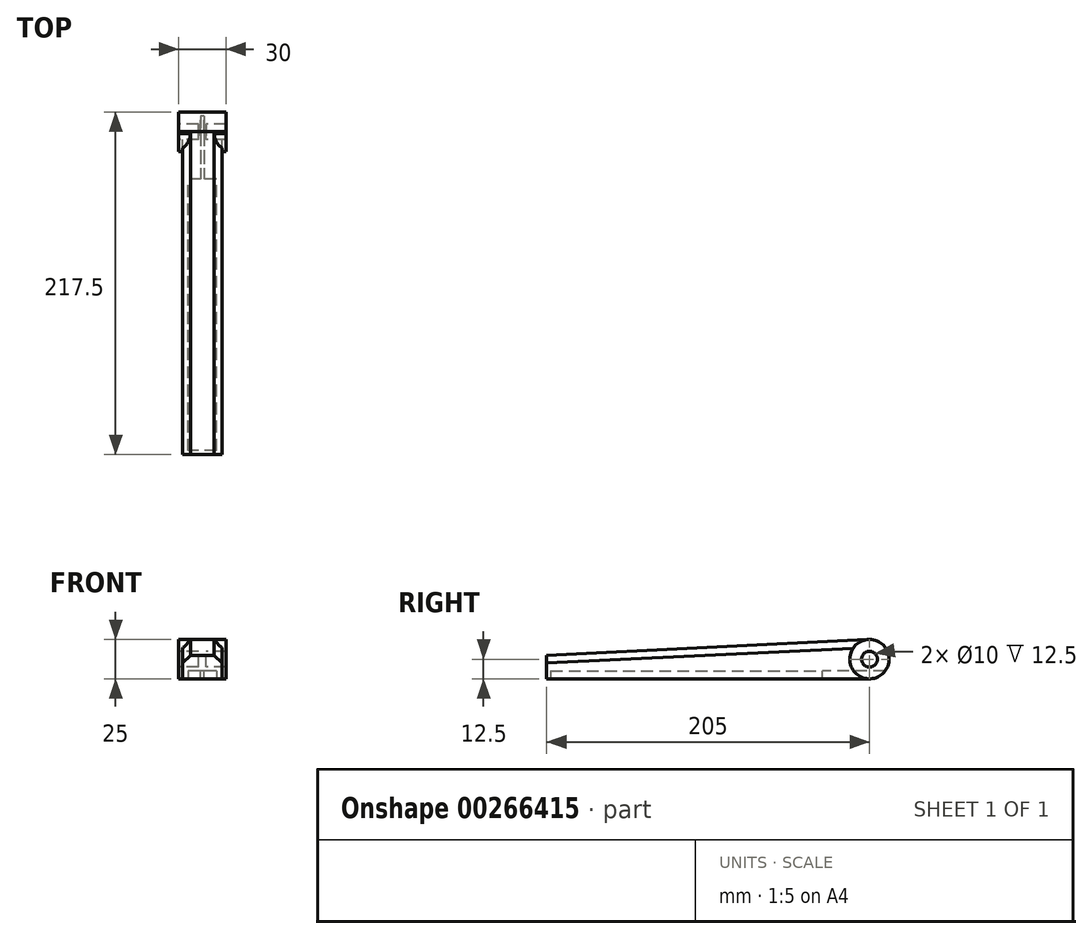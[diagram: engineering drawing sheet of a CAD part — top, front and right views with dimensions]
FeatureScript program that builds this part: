
annotation { "Feature Type Name" : "Feature", "Feature Type Description" : "" }
export const myFeature = defineFeature(function(context is Context, id is Id, definition is map)
    precondition{}
    {
        {
            var Q0;
            Q0=qCreatedBy(makeId("Right.planeOp"),FACE);
            var sketch = newSketch(context, id + "F0", { "sketchPlane" : qUnion([Q0])});
            skCircle(sketch, "E0", {"center": v(97.5, -2.5) * mm, "radius": 12.5 * mm});
            skLineSegment(sketch, "E1", {"start": v(97.5, 10) * mm, "end": v(-107.5, 0) * mm});
            skCircle(sketch, "E2", {"center": v(97.5, -2.5) * mm, "radius": 5 * mm});
            skLineSegment(sketch, "E3", {"start": v(97.5, -15) * mm, "end": v(-107.5, -15) * mm});
            skLineSegment(sketch, "E4", {"start": v(-107.5, 0) * mm, "end": v(-107.5, -15) * mm});
            skSolve(sketch);
        }
        {
            var Q0;
            Q0=makeQuery(id+"F0.imprint","IMPRINT",FACE,{"disambiguationData":[TD([[makeQuery(id+"F0.imprint","IMPRINT",EDGE,{"derivedFrom":sQuery(id+"F0.wireOp",EDGE,"E2")}),-1.0]])]});
            extrude(context, id + "F1", {"entities" : qUnion([Q0]), "depth" : 15 * mm, "hasSecondDirection" : true, "secondDirectionOppositeDirection" : true, "secondDirectionDepth" : 15 * mm, "offsetDistance" : 25 * mm});
        }
        {
            var Q0;
            {var subQ0=sQuery(id+"F0.wireOp",EDGE,"E3");Q0=makeQuery(id+"F0.imprint","IMPRINT",FACE,{"disambiguationData":[TD([[makeQuery(id+"F0.imprint","IMPRINT",EDGE,{"derivedFrom":subQ0}),-1.0]])]});}
            extrude(context, id + "F2", {"entities" : qUnion([Q0]), "operationType" : NewBodyOperationType.ADD, "depth" : 12.5 * mm, "hasSecondDirection" : true, "secondDirectionOppositeDirection" : true, "secondDirectionDepth" : 12.5 * mm, "offsetDistance" : 25 * mm});
        }
        {
            var Q0;
            Q0=makeQuery(id+"F2.opExtrude","SWEPT_FACE",FACE,{"disambiguationData":[OSD([sQuery(id+"F0.wireOp",EDGE,"E3")])]});
            var sketch = newSketch(context, id + "F3", { "sketchPlane" : qUnion([Q0])});
            skLineSegment(sketch, "E5", {"start": v(9, 105) * mm, "end": v(-9, 105) * mm});
            skLineSegment(sketch, "E6", {"start": v(-9, 105) * mm, "end": v(-9, -95) * mm});
            skLineSegment(sketch, "E7", {"start": v(9, 105) * mm, "end": v(9, -95) * mm});
            skLineSegment(sketch, "E8", {"start": v(9, -95) * mm, "end": v(-9, -95) * mm});
            skLineSegment(sketch, "E9", {"start": v(0, -95) * mm, "end": v(0, -67.5) * mm, "construction": true});
            skLineSegment(sketch, "E10", {"start": v(0, -67.5) * mm, "end": v(9, -67.5) * mm});
            skLineSegment(sketch, "E11", {"start": v(0, -67.5) * mm, "end": v(-9, -67.5) * mm});
            skSolve(sketch);
        }
        {
            var Q0;
            Q0=makeQuery(id+"F3.imprint","IMPRINT",FACE,{"disambiguationData":[TD([[makeQuery(id+"F3.imprint","IMPRINT",EDGE,{"derivedFrom":sQuery(id+"F3.wireOp",EDGE,"E5")}),1.0]])]});
            extrude(context, id + "F4", {"entities" : qUnion([Q0]), "operationType" : NewBodyOperationType.REMOVE, "oppositeDirection" : true, "depth" : 5 * mm});
        }
        {
            var Q0;
            Q0=makeQuery(id+"F4.boolean.opBoolean","COPY",FACE,{"derivedFrom":makeQuery(id+"F4.opExtrude","SWEPT_FACE",FACE,{"disambiguationData":[OSD([sQuery(id+"F3.wireOp",EDGE,"E10"),sQuery(id+"F3.wireOp",EDGE,"E11")])]})});
            var sketch = newSketch(context, id + "F5", { "sketchPlane" : qUnion([Q0])});
            skLineSegment(sketch, "E12", {"start": v(0, -10) * mm, "end": v(0, -15) * mm, "construction": true});
            skLineSegment(sketch, "E13", {"start": v(0, -15) * mm, "end": v(-1, -15) * mm});
            skLineSegment(sketch, "E14", {"start": v(0, -15) * mm, "end": v(1, -15) * mm});
            skLineSegment(sketch, "E15", {"start": v(-1, -15) * mm, "end": v(-1, -10) * mm});
            skLineSegment(sketch, "E16", {"start": v(-1, -10) * mm, "end": v(0, -10) * mm});
            skLineSegment(sketch, "E17", {"start": v(1, -15) * mm, "end": v(1, -10) * mm});
            skLineSegment(sketch, "E18", {"start": v(1, -10) * mm, "end": v(0, -10) * mm});
            skSolve(sketch);
        }
        {
            var Q0;
            Q0=makeQuery(id+"F5.imprint","IMPRINT",FACE,{"disambiguationData":[TD([[makeQuery(id+"F5.imprint","IMPRINT",EDGE,{"derivedFrom":sQuery(id+"F5.wireOp",EDGE,"E13")}),-1.0]])]});
            extrude(context, id + "F6", {"entities" : qUnion([Q0]), "operationType" : NewBodyOperationType.REMOVE, "endBound" : BoundingType.THROUGH_ALL, "oppositeDirection" : true, "depth" : 25 * mm, "offsetDistance" : 25 * mm});
        }
        {
            var Q0;
            Q0=makeQuery(id+"F2.opExtrude","CAP_EDGE",EDGE,{"disambiguationData":[OSD([sQuery(id+"F0.wireOp",EDGE,"E1")])],"isStart":true});
            var Q1;
            Q1=makeQuery(id+"F2.opExtrude","CAP_EDGE",EDGE,{"disambiguationData":[OSD([sQuery(id+"F0.wireOp",EDGE,"E1")])],"isStart":false});
            chamfer(context, id + "F7", {"entities" : qUnion([Q0, Q1]), "width" : 5 * mm, "tangentPropagation" : true});
        }
        {
            var Q0;
            Q0=makeQuery(id+"F0.imprint","IMPRINT",FACE,{"disambiguationData":[TD([[makeQuery(id+"F0.imprint","IMPRINT",EDGE,{"derivedFrom":sQuery(id+"F0.wireOp",EDGE,"E2")}),1.0]])]});
            extrude(context, id + "F8", {"entities" : qUnion([Q0]), "operationType" : NewBodyOperationType.ADD, "depth" : 2.5 * mm, "offsetDistance" : 25 * mm, "hasSecondDirection" : true, "secondDirectionOppositeDirection" : true, "secondDirectionDepth" : 2.5 * mm});
        }
    });
